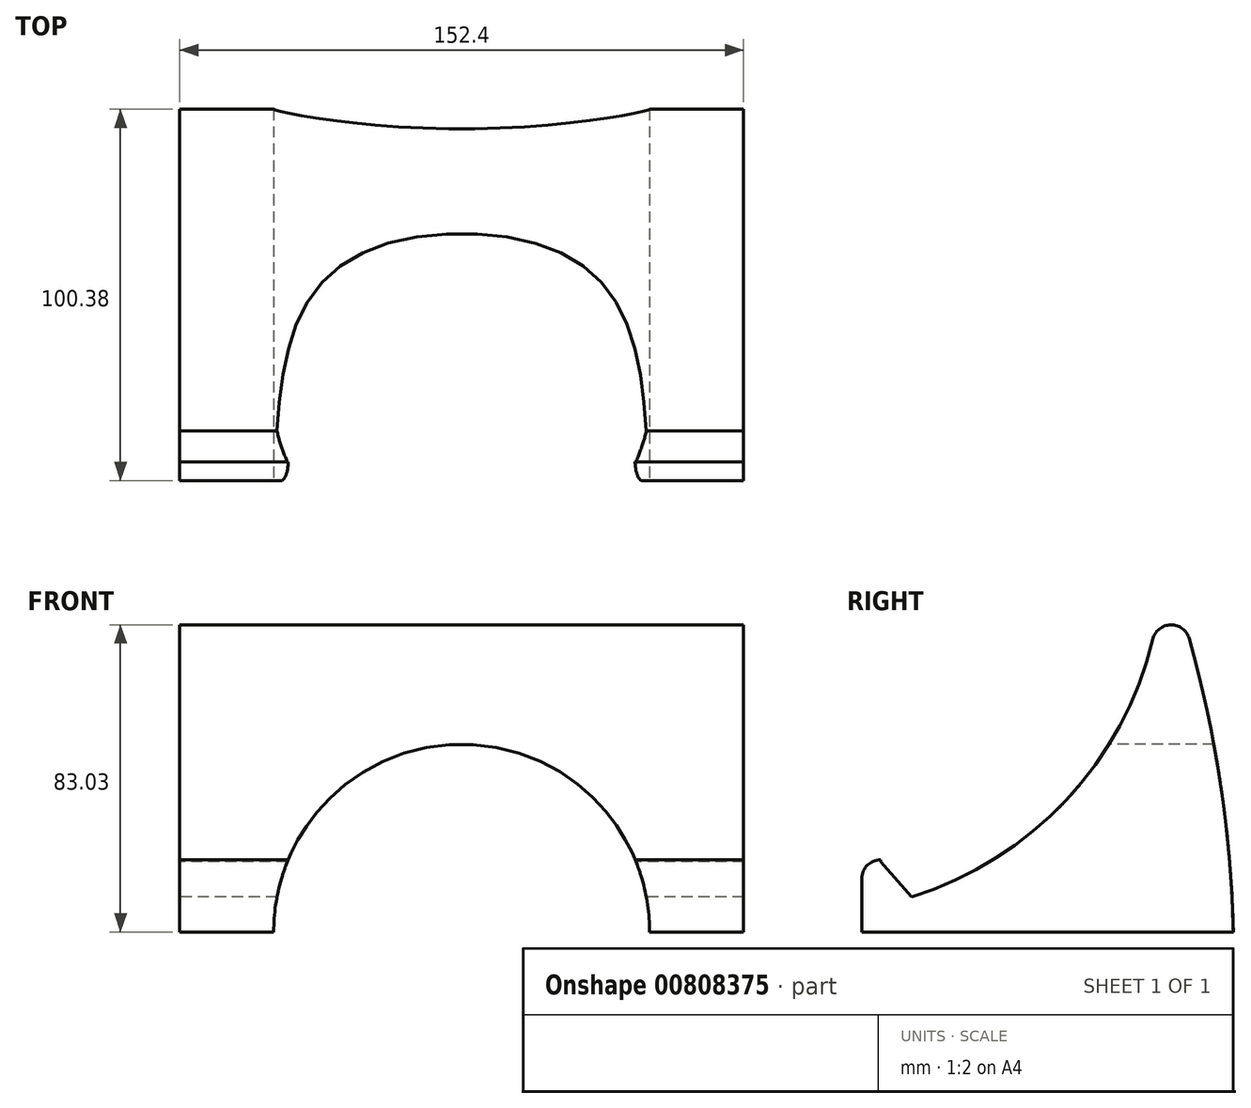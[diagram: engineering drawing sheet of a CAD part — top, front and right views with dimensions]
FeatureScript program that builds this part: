
annotation { "Feature Type Name" : "Feature", "Feature Type Description" : "" }
export const myFeature = defineFeature(function(context is Context, id is Id, definition is map)
    precondition{}
    {
        {
            var Q0;
            Q0=qCreatedBy(makeId("Right.planeOp"),FACE);
            var sketch = newSketch(context, id + "F0", { "sketchPlane" : qUnion([Q0])});
            skLineSegment(sketch, "E0", {"start": v(-36.99, 5.2) * mm, "end": v(-36.99, -13.84) * mm});
            skLineSegment(sketch, "E1", {"start": v(-36.99, -13.84) * mm, "end": v(39.21, -13.84) * mm});
            skLineSegment(sketch, "E2", {"start": v(39.21, -13.84) * mm, "end": v(39.21, 87.76) * mm});
            skLineSegment(sketch, "E3", {"start": v(-36.99, 5.2) * mm, "end": v(-28.64, -4.36) * mm});
            skLineSegment(sketch, "E4.bottom", {"start": v(39.21, 87.76) * mm, "end": v(58.4, 87.76) * mm});
            skLineSegment(sketch, "E4.top", {"start": v(39.21, -13.84) * mm, "end": v(58.4, -13.84) * mm});
            skLineSegment(sketch, "E4.left", {"start": v(39.21, 87.76) * mm, "end": v(39.21, -13.84) * mm});
            skLineSegment(sketch, "E4.right", {"start": v(58.4, 87.76) * mm, "end": v(58.4, -13.84) * mm});
            skArc(sketch, "E5", {"start": v(-28.64, -4.36) * mm, "mid": v(20.42, 30.55) * mm, "end": v(39.21, 87.76) * mm});
            skLineSegment(sketch, "E6.bottom", {"start": v(-36.99, -13.84) * mm, "end": v(-42.07, -13.84) * mm});
            skLineSegment(sketch, "E6.top", {"start": v(-36.99, 5.7) * mm, "end": v(-42.07, 5.7) * mm});
            skLineSegment(sketch, "E6.left", {"start": v(-36.99, -13.84) * mm, "end": v(-36.99, 5.7) * mm});
            skLineSegment(sketch, "E6.right", {"start": v(-42.07, -13.84) * mm, "end": v(-42.07, 5.7) * mm});
            skSolve(sketch);
        }
        {
            var Q0;
            Q0 = qSketchRegion(id + "F0", true);
            extrude(context, id + "F1", {"entities" : qUnion([Q0]), "endBound" : BoundingType.SYMMETRIC, "depth" : 152.4 * mm, "offsetDistance" : 25.4 * mm});
        }
        {
            var Q0;
            Q0=qCreatedBy(makeId("Front.planeOp"),FACE);
            var sketch = newSketch(context, id + "F2", { "sketchPlane" : qUnion([Q0])});
            skArc(sketch, "E7", {"start": v(-50.8, -13.87) * mm, "mid": v(0.15, 36.93) * mm, "end": v(50.8, -14.17) * mm});
            skLineSegment(sketch, "E8", {"start": v(-50.8, -13.87) * mm, "end": v(50.8, -14.17) * mm});
            skSolve(sketch);
        }
        {
            var Q0;
            Q0 = qSketchRegion(id + "F2", true);
            extrude(context, id + "F3", {"entities" : qUnion([Q0]), "operationType" : NewBodyOperationType.REMOVE, "endBound" : BoundingType.SYMMETRIC, "oppositeDirection" : true, "depth" : 134.62 * mm, "offsetDistance" : 25.4 * mm});
        }
        {
            var Q0;
            Q0=makeQuery(id+"F1.opExtrude","SWEPT_EDGE",EDGE,{"disambiguationData":[OSD([sQuery(id+"F0.wireOp",EDGE,"E4.bottom"),sQuery(id+"F0.wireOp",EDGE,"E4.right")])]});
            fillet(context, id + "F4", {"entities" : qUnion([Q0]), "radius" : 319.48 * mm, "tangentPropagation" : true, "allowEdgeOverflow" : false});
        }
        {
            var Q0;
            {var subQ0=sQuery(id+"F0.wireOp",EDGE,"E6.right");var subQ1=sQuery(id+"F0.wireOp",EDGE,"E6.top");Q0=makeQuery(id+"F3.boolean.opBoolean","SPLIT",EDGE,{"disambiguationData":[TD([makeQuery(id+"F1.opExtrude","CAP_FACE",FACE,{"disambiguationData":[OSD([sQuery(id+"F0.wireOp",EDGE,"E1"),sQuery(id+"F0.wireOp",EDGE,"E3"),sQuery(id+"F0.wireOp",EDGE,"E4.bottom"),sQuery(id+"F0.wireOp",EDGE,"E4.top"),sQuery(id+"F0.wireOp",EDGE,"E4.right"),sQuery(id+"F0.wireOp",EDGE,"E5"),sQuery(id+"F0.wireOp",EDGE,"E6.bottom"),subQ1,sQuery(id+"F0.wireOp",EDGE,"E6.left"),subQ0])],"isStart":true})])],"derivedFrom":makeQuery(id+"F1.opExtrude","SWEPT_EDGE",EDGE,{"disambiguationData":[OSD([subQ1,subQ0])]})});}
            var Q1;
            {var subQ0=sQuery(id+"F0.wireOp",EDGE,"E6.right");var subQ1=sQuery(id+"F0.wireOp",EDGE,"E6.top");Q1=makeQuery(id+"F3.boolean.opBoolean","SPLIT",EDGE,{"disambiguationData":[TD([makeQuery(id+"F1.opExtrude","CAP_FACE",FACE,{"disambiguationData":[OSD([sQuery(id+"F0.wireOp",EDGE,"E1"),sQuery(id+"F0.wireOp",EDGE,"E3"),sQuery(id+"F0.wireOp",EDGE,"E4.bottom"),sQuery(id+"F0.wireOp",EDGE,"E4.top"),sQuery(id+"F0.wireOp",EDGE,"E4.right"),sQuery(id+"F0.wireOp",EDGE,"E5"),sQuery(id+"F0.wireOp",EDGE,"E6.bottom"),subQ1,sQuery(id+"F0.wireOp",EDGE,"E6.left"),subQ0])],"isStart":false})])],"derivedFrom":makeQuery(id+"F1.opExtrude","SWEPT_EDGE",EDGE,{"disambiguationData":[OSD([subQ1,subQ0])]})});}
            fillet(context, id + "F5", {"entities" : qUnion([Q0, Q1]), "radius" : 5.08 * mm, "tangentPropagation" : true, "allowEdgeOverflow" : false});
        }
        {
            var Q0;
            Q0=makeQuery(id+"F4.opFillet","BLEND_EDGE",EDGE,{"blendedFrom":[makeQuery(id+"F1.opExtrude","SWEPT_EDGE",EDGE,{"disambiguationData":[OSD([sQuery(id+"F0.wireOp",EDGE,"E4.bottom"),sQuery(id+"F0.wireOp",EDGE,"E4.right")])]}),makeQuery(id+"F1.opExtrude","SWEPT_FACE",FACE,{"disambiguationData":[OSD([sQuery(id+"F0.wireOp",EDGE,"E5")])]})],"blendedInto":[makeQuery(id+"F1.opExtrude","SWEPT_FACE",FACE,{"disambiguationData":[OSD([sQuery(id+"F0.wireOp",EDGE,"E5")])]})]});
            fillet(context, id + "F6", {"entities" : qUnion([Q0]), "radius" : 5.08 * mm, "tangentPropagation" : true, "allowEdgeOverflow" : false});
        }
    });
